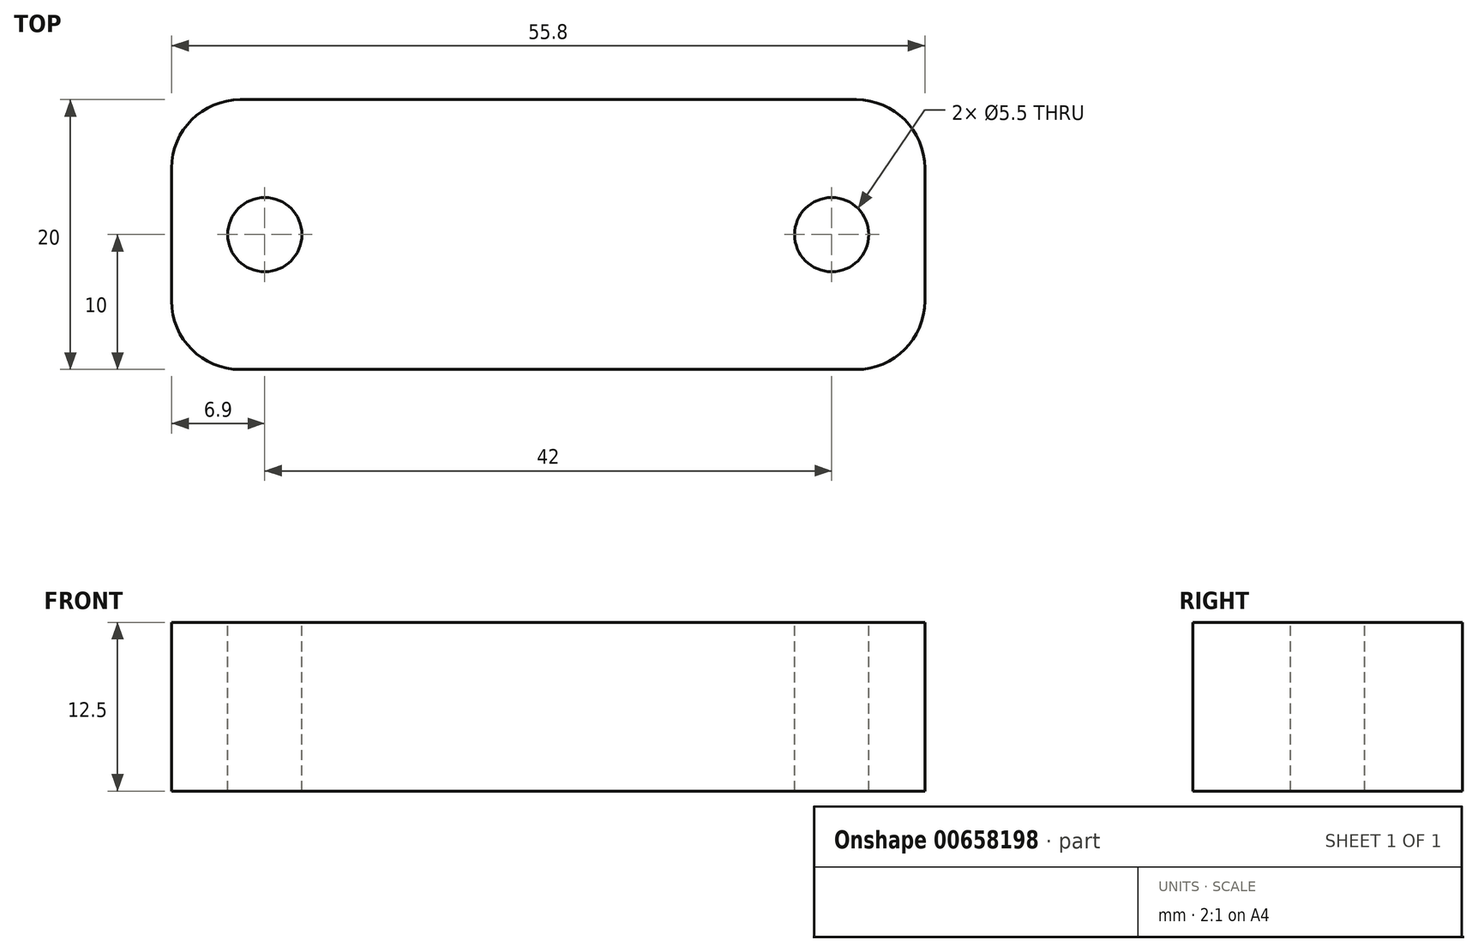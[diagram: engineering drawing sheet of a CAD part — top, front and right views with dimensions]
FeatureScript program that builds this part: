
annotation { "Feature Type Name" : "Feature", "Feature Type Description" : "" }
export const myFeature = defineFeature(function(context is Context, id is Id, definition is map)
    precondition{}
    {
        {
            var Q0;
            Q0=qCreatedBy(makeId("Top.planeOp"),FACE);
            var sketch = newSketch(context, id + "F0", { "sketchPlane" : qUnion([Q0])});
            skLineSegment(sketch, "E0.bottom", {"start": v(27.9, -10) * mm, "end": v(-27.9, -10) * mm});
            skLineSegment(sketch, "E0.top", {"start": v(27.9, 10) * mm, "end": v(-27.9, 10) * mm});
            skLineSegment(sketch, "E0.left", {"start": v(27.9, -10) * mm, "end": v(27.9, 10) * mm});
            skLineSegment(sketch, "E0.right", {"start": v(-27.9, -10) * mm, "end": v(-27.9, 10) * mm});
            skPoint(sketch, "E0.middle", {"position": v(0, 0) * mm});
            skPoint(sketch, "E1", {"position": v(21, 0) * mm});
            skPoint(sketch, "E2.MirrorP", {"position": v(-21, 0) * mm});
            skSolve(sketch);
        }
        {
            var Q0;
            Q0=makeQuery(id+"F0.imprint","IMPRINT",FACE,{"disambiguationData":[TD([[makeQuery(id+"F0.imprint","IMPRINT",EDGE,{"derivedFrom":sQuery(id+"F0.wireOp",EDGE,"E0.bottom")}),-1.0]])]});
            extrude(context, id + "F1", {"entities" : qUnion([Q0]), "oppositeDirection" : true, "depth" : 12.5 * mm, "offsetDistance" : 25.4 * mm});
        }
        {
            var Q0;
            Q0=sQuery(id+"F0.wireOp",VERTEX,"E1");
            var Q1;
            Q1=sQuery(id+"F0.wireOp",VERTEX,"E2.MirrorP");
            var Q2;
            Q2=makeQuery(id+"F1.opExtrude","SWEPT_BODY",BODY,{"disambiguationData":[OSD([sQuery(id+"F0.wireOp",EDGE,"E0.bottom"),sQuery(id+"F0.wireOp",EDGE,"E0.top"),sQuery(id+"F0.wireOp",EDGE,"E0.left"),sQuery(id+"F0.wireOp",EDGE,"E0.right")])]});
            hole(context, id + "F2", {"style" : HoleStyle.SIMPLE, "endStyle" : HoleEndStyle.THROUGH, "standardTappedOrClearance" : lookupTablePath({ "standard" : "ISO", "fit" : "Normal", "size" : "M5", "type" : "Clearance" }), "standardBlindInLast" : lookupTablePath({ "fit" : "Standard", "standard" : "ISO", "size" : "M5", "type" : "Clearance" }), "holeDiameter" : 5.5 * mm, "majorDiameter" : 3 * mm, "isTappedThrough" : true, "tappedDepth" : 12.7 * mm, "tapClearance" : 3, "locations" : qUnion([Q0, Q1]), "scope" : qUnion([Q2])});
        }
        {
            var Q0;
            Q0=makeQuery(id+"F1.opExtrude","SWEPT_EDGE",EDGE,{"disambiguationData":[OSD([sQuery(id+"F0.wireOp",EDGE,"E0.top"),sQuery(id+"F0.wireOp",EDGE,"E0.left")])]});
            var Q1;
            Q1=makeQuery(id+"F1.opExtrude","SWEPT_EDGE",EDGE,{"disambiguationData":[OSD([sQuery(id+"F0.wireOp",EDGE,"E0.bottom"),sQuery(id+"F0.wireOp",EDGE,"E0.left")])]});
            var Q2;
            Q2=makeQuery(id+"F1.opExtrude","SWEPT_EDGE",EDGE,{"disambiguationData":[OSD([sQuery(id+"F0.wireOp",EDGE,"E0.bottom"),sQuery(id+"F0.wireOp",EDGE,"E0.right")])]});
            var Q3;
            Q3=makeQuery(id+"F1.opExtrude","SWEPT_EDGE",EDGE,{"disambiguationData":[OSD([sQuery(id+"F0.wireOp",EDGE,"E0.top"),sQuery(id+"F0.wireOp",EDGE,"E0.right")])]});
            fillet(context, id + "F3", {"entities" : qUnion([Q0, Q1, Q2, Q3]), "radius" : 5.08 * mm, "tangentPropagation" : true, "allowEdgeOverflow" : false});
        }
    });
